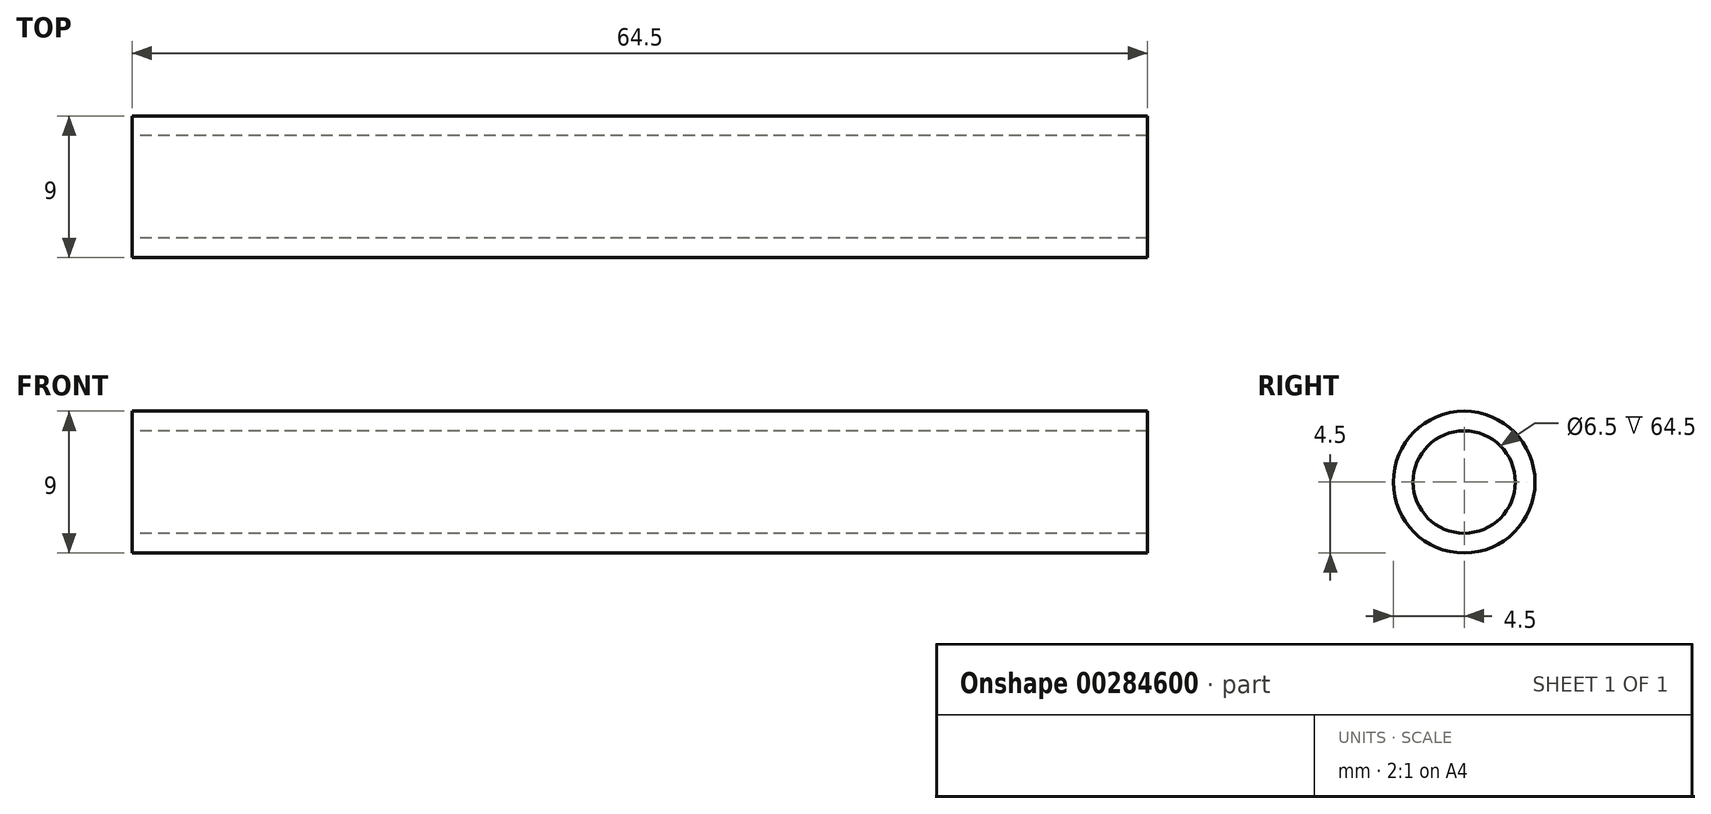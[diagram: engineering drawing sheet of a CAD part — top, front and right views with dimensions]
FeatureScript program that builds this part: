
annotation { "Feature Type Name" : "Feature", "Feature Type Description" : "" }
export const myFeature = defineFeature(function(context is Context, id is Id, definition is map)
    precondition{}
    {
        {
            var Q0;
            Q0=qCreatedBy(makeId("Right.planeOp"),FACE);
            var sketch = newSketch(context, id + "F0", { "sketchPlane" : qUnion([Q0])});
            skCircle(sketch, "E0", {"center": v(0, 0) * mm, "radius": 4.5 * mm});
            skCircle(sketch, "E1", {"center": v(0, 0) * mm, "radius": 3.25 * mm});
            skSolve(sketch);
        }
        {
            var Q0;
            Q0=qSketchRegion(id+"F0",true);
            extrude(context, id + "F1", {"entities" : qUnion([Q0]), "depth" : 64.5 * mm});
        }
    });
